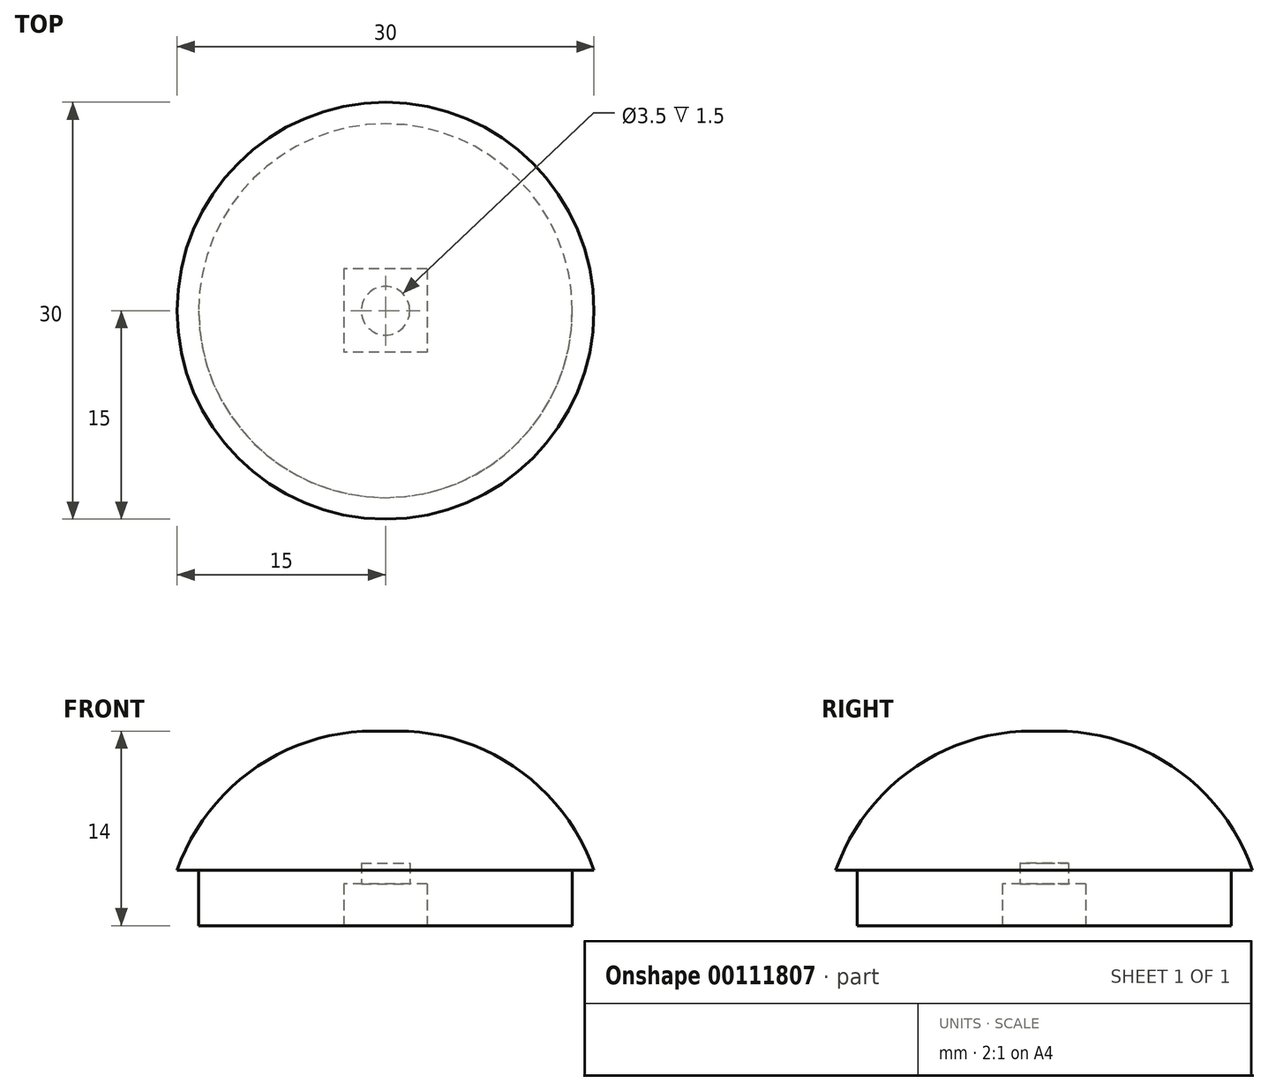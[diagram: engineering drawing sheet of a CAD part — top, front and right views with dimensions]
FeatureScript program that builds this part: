
annotation { "Feature Type Name" : "Feature", "Feature Type Description" : "" }
export const myFeature = defineFeature(function(context is Context, id is Id, definition is map)
    precondition{}
    {
        {
            var Q0;
            Q0=qCreatedBy(makeId("Top.planeOp"),FACE);
            var sketch = newSketch(context, id + "F0", { "sketchPlane" : qUnion([Q0])});
            skCircle(sketch, "E0", {"center": v(0, 0) * mm, "radius": 15 * mm});
            skSolve(sketch);
        }
        {
            var Q0;
            Q0 = qSketchRegion(id + "F0", true);
            extrude(context, id + "F1", {"entities" : qUnion([Q0]), "depth" : 10 * mm});
        }
        {
            var Q0;
            Q0=makeQuery(id+"F1.opExtrude","CAP_FACE",FACE,{"disambiguationData":[OSD([sQuery(id+"F0.wireOp",EDGE,"E0")])],"isStart":false});
            fillet(context, id + "F2", {"entities" : qUnion([Q0]), "radius" : 15 * mm, "tangentPropagation" : true, "allowEdgeOverflow" : false});
        }
        {
            var Q0;
            Q0=makeQuery(id+"F1.opExtrude","CAP_FACE",FACE,{"disambiguationData":[OSD([sQuery(id+"F0.wireOp",EDGE,"E0")])],"isStart":true});
            var sketch = newSketch(context, id + "F3", { "sketchPlane" : qUnion([Q0])});
            skCircle(sketch, "E1", {"center": v(0, 0) * mm, "radius": 13.45 * mm});
            skSolve(sketch);
        }
        {
            var Q0;
            Q0=makeQuery(id+"F3.imprint","IMPRINT",FACE,{"disambiguationData":[TD([[makeQuery(id+"F3.imprint","IMPRINT",EDGE,{"derivedFrom":sQuery(id+"F3.wireOp",EDGE,"E1")}),1.0]])]});
            extrude(context, id + "F4", {"entities" : qUnion([Q0]), "operationType" : NewBodyOperationType.ADD, "depth" : 4 * mm});
        }
        {
            var Q0;
            Q0=makeQuery(id+"F4.opExtrude","CAP_FACE",FACE,{"disambiguationData":[OSD([sQuery(id+"F3.wireOp",EDGE,"E1")])],"isStart":false});
            var sketch = newSketch(context, id + "F5", { "sketchPlane" : qUnion([Q0])});
            skLineSegment(sketch, "E2.bottom", {"start": v(3, -3) * mm, "end": v(-3, -3) * mm});
            skLineSegment(sketch, "E2.top", {"start": v(3, 3) * mm, "end": v(-3, 3) * mm});
            skLineSegment(sketch, "E2.left", {"start": v(3, -3) * mm, "end": v(3, 3) * mm});
            skLineSegment(sketch, "E2.right", {"start": v(-3, -3) * mm, "end": v(-3, 3) * mm});
            skPoint(sketch, "E2.middle", {"position": v(0, 0) * mm});
            skSolve(sketch);
        }
        {
            var Q0;
            Q0=makeQuery(id+"F5.imprint","IMPRINT",FACE,{"disambiguationData":[TD([[makeQuery(id+"F5.imprint","IMPRINT",EDGE,{"derivedFrom":sQuery(id+"F5.wireOp",EDGE,"E2.bottom")}),-1.0]])]});
            extrude(context, id + "F6", {"entities" : qUnion([Q0]), "operationType" : NewBodyOperationType.REMOVE, "oppositeDirection" : true, "depth" : 3 * mm});
        }
        {
            var Q0;
            Q0=makeQuery(id+"F6.boolean.opBoolean","COPY",FACE,{"derivedFrom":makeQuery(id+"F6.opExtrude","CAP_FACE",FACE,{"disambiguationData":[OSD([sQuery(id+"F5.wireOp",EDGE,"E2.bottom"),sQuery(id+"F5.wireOp",EDGE,"E2.top"),sQuery(id+"F5.wireOp",EDGE,"E2.left"),sQuery(id+"F5.wireOp",EDGE,"E2.right")])],"isStart":false})});
            var sketch = newSketch(context, id + "F7", { "sketchPlane" : qUnion([Q0])});
            skCircle(sketch, "E3", {"center": v(0, 0) * mm, "radius": 1.75 * mm});
            skSolve(sketch);
        }
        {
            var Q0;
            Q0=makeQuery(id+"F7.imprint","IMPRINT",FACE,{"disambiguationData":[TD([[makeQuery(id+"F7.imprint","IMPRINT",EDGE,{"derivedFrom":sQuery(id+"F7.wireOp",EDGE,"E3")}),1.0]])]});
            extrude(context, id + "F8", {"entities" : qUnion([Q0]), "operationType" : NewBodyOperationType.REMOVE, "oppositeDirection" : true, "depth" : 1.5 * mm});
        }
    });
